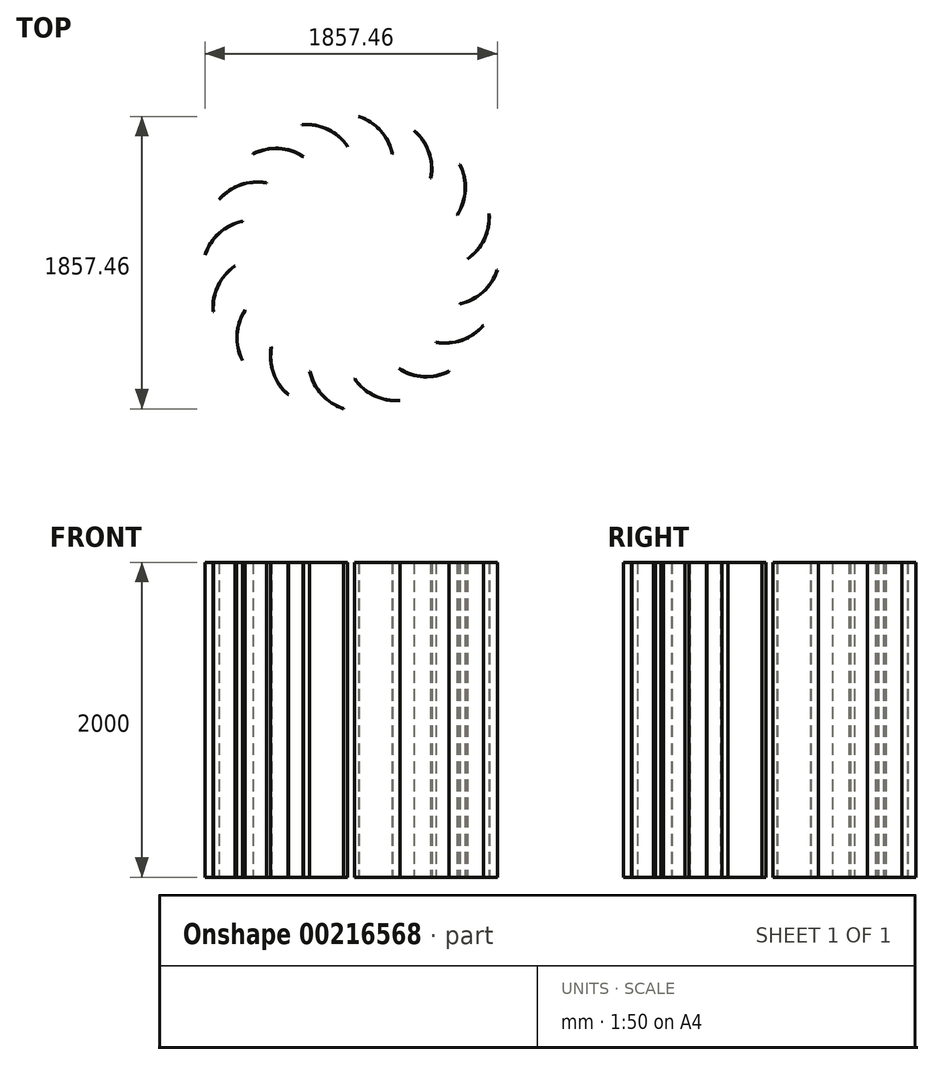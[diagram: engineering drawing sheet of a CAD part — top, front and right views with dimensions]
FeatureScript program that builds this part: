
annotation { "Feature Type Name" : "Feature", "Feature Type Description" : "" }
export const myFeature = defineFeature(function(context is Context, id is Id, definition is map)
    precondition{}
    {
        {
            var Q0;
            Q0=qCreatedBy(makeId("Top.planeOp"),FACE);
            var sketch = newSketch(context, id + "F0", { "sketchPlane" : qUnion([Q0])});
            skCircle(sketch, "E0", {"center": v(0, 0) * mm, "radius": 930 * mm, "construction": true});
            skLineSegment(sketch, "E1", {"start": v(0, 0) * mm, "end": v(-1129.93, 0) * mm, "construction": true});
            skLineSegment(sketch, "E2", {"start": v(-930, 0) * mm, "end": v(-928.07, -0.52) * mm});
            skLineSegment(sketch, "E3", {"start": v(0, 0) * mm, "end": v(-1030.68, 54.02) * mm, "construction": true});
            skPoint(sketch, "E4", {"position": v(-928.73, 48.67) * mm});
            skLineSegment(sketch, "E5", {"start": v(-928.73, 48.67) * mm, "end": v(-578.96, 363.6) * mm, "construction": true});
            skLineSegment(sketch, "E6", {"start": v(-928.73, 48.67) * mm, "end": v(-926.82, 48.05) * mm});
            skCircle(sketch, "E7", {"center": v(-928.73, 48.67) * mm, "radius": 280 * mm, "construction": true});
            skPoint(sketch, "E8", {"position": v(-662.43, -37.85) * mm});
            skPoint(sketch, "E9", {"position": v(-720.64, 236.03) * mm});
            skLineSegment(sketch, "E10", {"start": v(-720.64, 236.03) * mm, "end": v(-720.23, 234.07) * mm});
            skLineSegment(sketch, "E11.trimOffspring", {"start": v(-678.03, 35.53) * mm, "end": v(-662.43, -37.85) * mm});
            skLineSegment(sketch, "E12.trimOffspring", {"start": v(-778.93, 0) * mm, "end": v(-328.19, -146.45) * mm});
            skCircle(sketch, "E13", {"center": v(-928.73, 48.67) * mm, "radius": 320 * mm, "construction": true});
            skArc(sketch, "E14", {"start": v(-690.92, 262.8) * mm, "mid": v(-838.5, 187.6) * mm, "end": v(-928.73, 48.67) * mm});
            skArc(sketch, "E15", {"start": v(-690.5, 260.84) * mm, "mid": v(-837.17, 186.1) * mm, "end": v(-926.82, 48.05) * mm});
            skLineSegment(sketch, "E16", {"start": v(-624.39, -50.21) * mm, "end": v(-665.97, 145.42) * mm});
            skLineSegment(sketch, "E17.trimOffspring", {"start": v(-690.5, 260.84) * mm, "end": v(-690.92, 262.8) * mm});
            skSolve(sketch);
        }
        {
            var Q0;
            Q0=qSketchRegion(id+"F0",true);
            extrude(context, id + "F1", {"entities" : qUnion([Q0]), "depth" : 2000 * mm});
        }
        {
            var Q0;
            Q0=qCreatedBy(makeId("Front.planeOp"),FACE);
            var sketch = newSketch(context, id + "F2", { "sketchPlane" : qUnion([Q0])});
            skLineSegment(sketch, "E18", {"start": v(0, -1523.6) * mm, "end": v(0, 2528.93) * mm, "construction": true});
            skSolve(sketch);
        }
        {
            var Q0;
            Q0=makeQuery(id+"F1.opExtrude","SWEPT_BODY",BODY,{"disambiguationData":[OSD([sQuery(id+"F0.wireOp",EDGE,"E6"),sQuery(id+"F0.wireOp",EDGE,"E10"),sQuery(id+"F0.wireOp",EDGE,"xYgimzoz-oWi7-36zP-miJ9-nlTbJLKraV8z"),sQuery(id+"F0.wireOp",EDGE,"KWvoKD05-fxWy-cd5k-cys3-prn21N07ndKy")])]});
            var Q1;
            Q1=sQuery(id+"F2.wireOp",EDGE,"E18");
            circularPattern(context, id + "F3", {"entities" : qUnion([Q0]), "axis" : qUnion([Q1]), "angle" : 360 * degree, "instanceCount" : 16, "equalSpace" : true});
        }
    });
